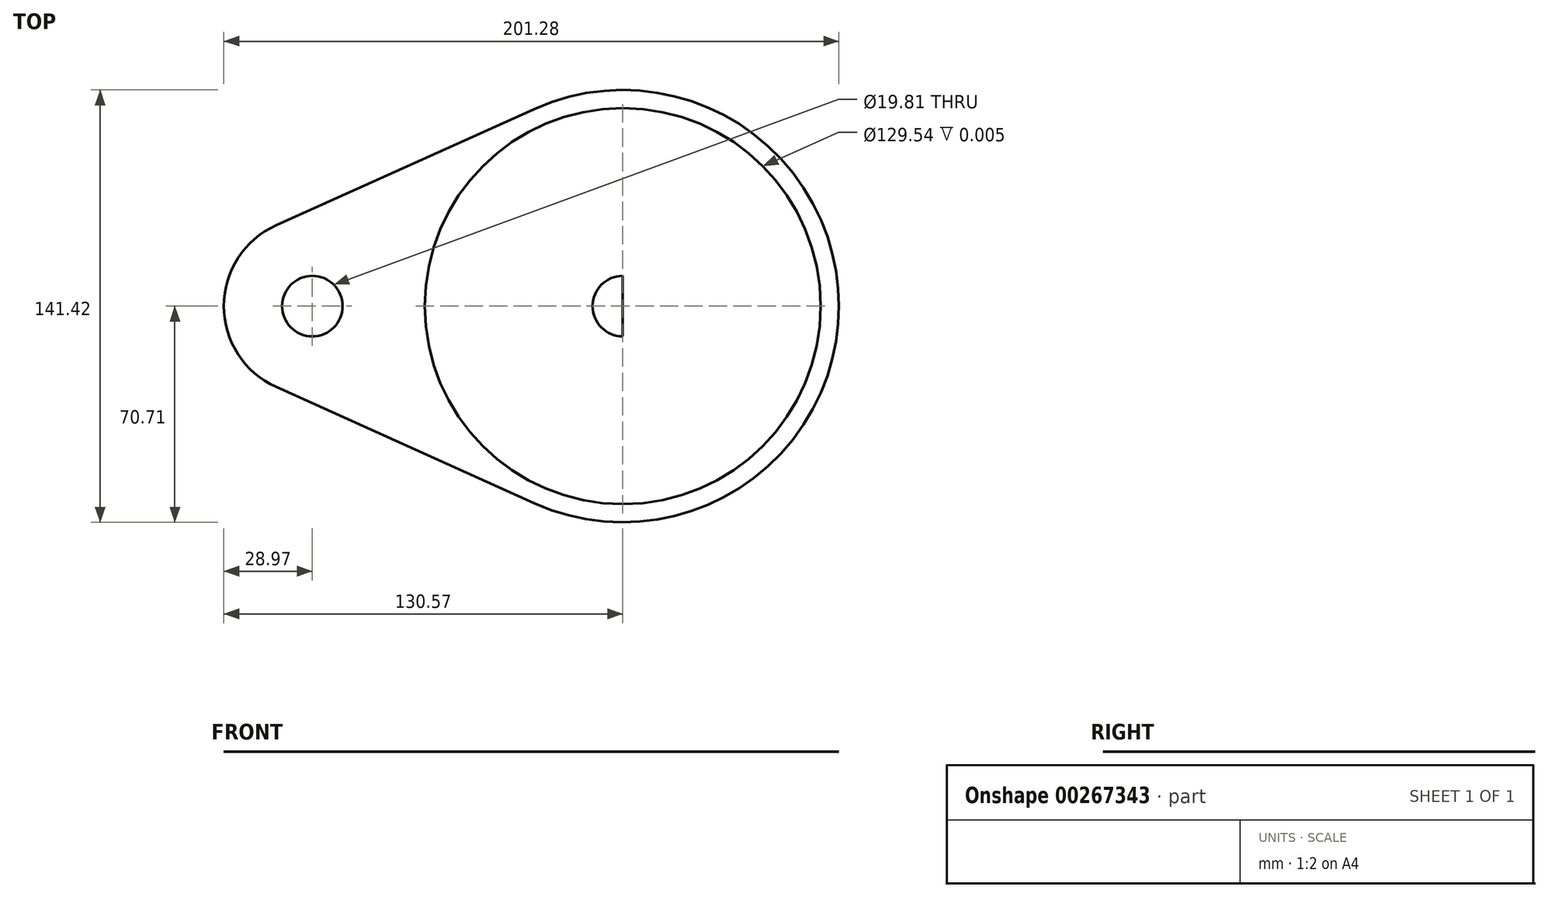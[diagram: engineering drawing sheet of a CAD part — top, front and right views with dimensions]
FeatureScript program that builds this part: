
annotation { "Feature Type Name" : "Feature", "Feature Type Description" : "" }
export const myFeature = defineFeature(function(context is Context, id is Id, definition is map)
    precondition{}
    {
        {
            var Q0;
            Q0=qCreatedBy(makeId("Top.planeOp"),FACE);
            var sketch = newSketch(context, id + "F0", { "sketchPlane" : qUnion([Q0])});
            skCircle(sketch, "E0", {"center": v(0, 0) * mm, "radius": 64.77 * mm});
            skLineSegment(sketch, "E1", {"start": v(0, 0) * mm, "end": v(-101.6, 0) * mm});
            skCircle(sketch, "E2", {"center": v(-101.6, 0) * mm, "radius": 13.9 * mm});
            skArc(sketch, "E3", {"start": v(-113.5, 26.41) * mm, "mid": v(-130.57, 0) * mm, "end": v(-113.5, -26.41) * mm});
            skArc(sketch, "E4", {"start": v(-29.05, -64.46) * mm, "mid": v(70.7, 0) * mm, "end": v(-29.05, 64.46) * mm});
            skLineSegment(sketch, "E5", {"start": v(-113.5, 26.41) * mm, "end": v(-29.05, 64.46) * mm});
            skLineSegment(sketch, "E6", {"start": v(-113.5, -26.41) * mm, "end": v(-29.05, -64.46) * mm});
            skLineSegment(sketch, "E7", {"start": v(0, 64.77) * mm, "end": v(0, -64.77) * mm});
            skPoint(sketch, "E8.MirrorCS.end.orphan", {"position": v(29.05, 64.46) * mm});
            skPoint(sketch, "E8.MirrorCS.start.orphan", {"position": v(113.5, 26.41) * mm});
            skPoint(sketch, "E9.MirrorCS.end.orphan", {"position": v(113.5, -26.41) * mm});
            skPoint(sketch, "E10.MirrorCS.end.orphan", {"position": v(29.05, -64.46) * mm});
            skCircle(sketch, "E11", {"center": v(-101.6, 0) * mm, "radius": 9.9 * mm});
            skCircle(sketch, "E12", {"center": v(0, 0) * mm, "radius": 9.9 * mm});
            skSolve(sketch);
        }
        {
            var Q0;
            Q0=makeQuery(id+"F0.imprint","IMPRINT",FACE,{"disambiguationData":[TD([[makeQuery(id+"F0.imprint","IMPRINT",EDGE,{"derivedFrom":sQuery(id+"F0.wireOp",EDGE,"E2")}),-1.0]])]});
            var Q1;
            Q1=makeQuery(id+"F0.imprint","IMPRINT",FACE,{"disambiguationData":[TD([[makeQuery(id+"F0.imprint","IMPRINT",EDGE,{"derivedFrom":sQuery(id+"F0.wireOp",EDGE,"E2")}),1.0]])]});
            var Q2;
            {var subQ0=sQuery(id+"F0.wireOp",EDGE,"E0");var subQ1=sQuery(id+"F0.wireOp",EDGE,"E1");var subQ2=makeQuery(id+"F0.imprint","INTERSECT",VERTEX,{"derivedFrom":[subQ1,subQ0]});Q2=makeQuery(id+"F0.imprint","IMPRINT",FACE,{"disambiguationData":[TD([[makeQuery(id+"F0.imprint","IMPRINT",EDGE,{"disambiguationData":[TD([[subQ2,1.0]])],"derivedFrom":subQ1}),-1.0]])]});}
            var Q3;
            {var subQ0=sQuery(id+"F0.wireOp",EDGE,"E0");var subQ1=sQuery(id+"F0.wireOp",EDGE,"E1");var subQ2=makeQuery(id+"F0.imprint","INTERSECT",VERTEX,{"derivedFrom":[subQ1,subQ0]});Q3=makeQuery(id+"F0.imprint","IMPRINT",FACE,{"disambiguationData":[TD([[makeQuery(id+"F0.imprint","IMPRINT",EDGE,{"disambiguationData":[TD([[subQ2,1.0]])],"derivedFrom":subQ1}),1.0]])]});}
            var Q4;
            {var subQ0=sQuery(id+"F0.wireOp",EDGE,"E0");var subQ1=sQuery(id+"F0.wireOp",EDGE,"E7");var subQ2=makeQuery(id+"F0.imprint","INTERSECT",VERTEX,{"disambiguationData":[OD(0.0)],"derivedFrom":[subQ1,subQ0]});Q4=makeQuery(id+"F0.imprint","IMPRINT",FACE,{"disambiguationData":[TD([[makeQuery(id+"F0.imprint","IMPRINT",EDGE,{"disambiguationData":[TD([[subQ2,-1.0]])],"derivedFrom":subQ1}),1.0]])]});}
            extrude(context, id + "F1", {"entities" : qUnion([Q0, Q1, Q2, Q3, Q4]), "depth" : 1 / 203.2 * mm});
        }
    });
